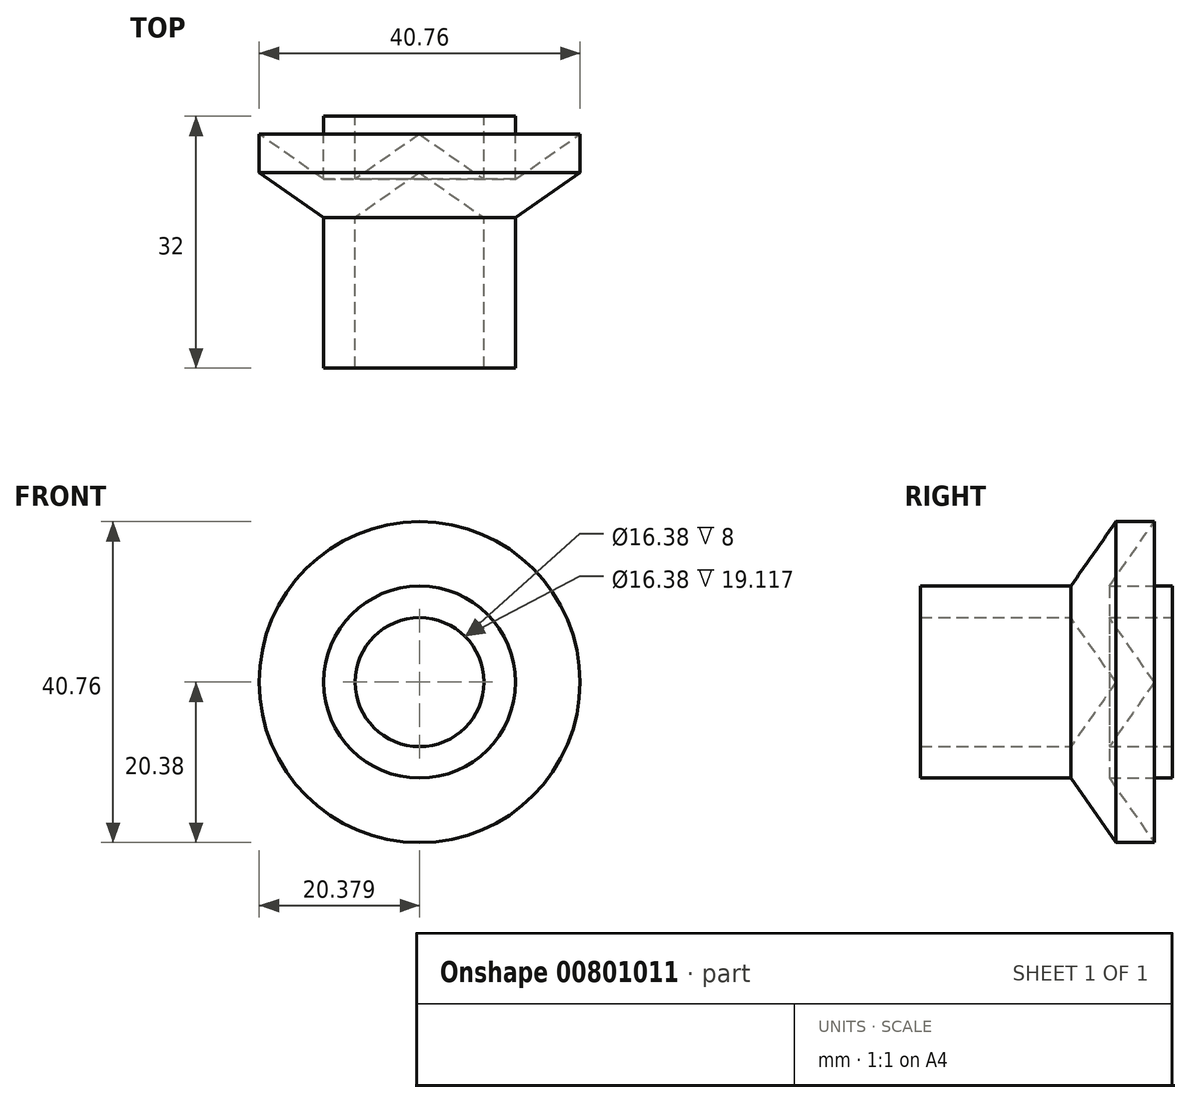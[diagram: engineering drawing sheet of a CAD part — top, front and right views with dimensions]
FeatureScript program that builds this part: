
annotation { "Feature Type Name" : "Feature", "Feature Type Description" : "" }
export const myFeature = defineFeature(function(context is Context, id is Id, definition is map)
    precondition{}
    {
        {
            var Q0;
            Q0=qCreatedBy(makeId("Top.planeOp"),FACE);
            var sketch = newSketch(context, id + "F0", { "sketchPlane" : qUnion([Q0])});
            skLineSegment(sketch, "E0", {"start": v(0, 0) * mm, "end": v(0, -8) * mm});
            skLineSegment(sketch, "E1", {"start": v(0, -8) * mm, "end": v(-8.2, -2.26) * mm});
            skLineSegment(sketch, "E2", {"start": v(-8.2, -2.26) * mm, "end": v(-8.2, -7.15) * mm});
            skLineSegment(sketch, "E3", {"start": v(-8.2, -7.15) * mm, "end": v(0, -12.88) * mm});
            skLineSegment(sketch, "E4", {"start": v(0, -12.88) * mm, "end": v(0, -32) * mm});
            skLineSegment(sketch, "E5", {"start": v(0, -32) * mm, "end": v(4, -32) * mm});
            skLineSegment(sketch, "E6", {"start": v(4, -32) * mm, "end": v(4, -12.88) * mm});
            skLineSegment(sketch, "E7", {"start": v(4, -8) * mm, "end": v(4, 0) * mm});
            skLineSegment(sketch, "E8", {"start": v(4, 0) * mm, "end": v(0, 0) * mm});
            skLineSegment(sketch, "E9", {"start": v(4, -8) * mm, "end": v(12.2, -2.26) * mm});
            skLineSegment(sketch, "E10", {"start": v(12.2, -2.26) * mm, "end": v(12.2, -7.15) * mm});
            skLineSegment(sketch, "E11", {"start": v(12.2, -7.15) * mm, "end": v(4, -12.88) * mm});
            skSolve(sketch);
        }
        {
            var Q0;
            Q0=makeQuery(id+"F0.imprint","IMPRINT",FACE,{"disambiguationData":[TD([[makeQuery(id+"F0.imprint","IMPRINT",EDGE,{"derivedFrom":sQuery(id+"F0.wireOp",EDGE,"E0")}),1.0]])]});
            var Q1;
            Q1=sQuery(id+"F0.wireOp",EDGE,"E2");
            revolve(context, id + "F1", {"surfaceOperationType" : NewSurfaceOperationType.NEW, "entities" : qUnion([Q0]), "axis" : qUnion([Q1]), "revolveType" : RevolveType.FULL});
        }
    });
